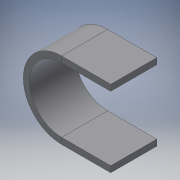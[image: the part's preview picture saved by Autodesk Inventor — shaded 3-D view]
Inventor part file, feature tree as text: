
AUTODESK INVENTOR PART (.ipt)
format: ipt  version: 2018 (Build 220112000, 112)  size: 137,216 bytes
history: native  units: mm
features: sheet_metal_op x3, other x2, sketch x1
ambient origin geometry x8: Origin, YZ Plane, XZ Plane, XY Plane, X Axis, Y Axis, Z Axis, Center Point
bodies: Solid1 (feature_tree)
feature tree (6):
  sheet_metal_op  "Contour Flange1"
  sketch  "Sketch1"  dims[d0=4.0mm d1=4.0mm d2=2.0mm d3=8.0mm d4=4.0mm d5=30.0mm d6=4.0mm d7=0.5mm d8=16.0mm d9=4.0mm d10=4.0mm d11=50.0mm d12=32.0mm]
  other  "Plate1"
  sheet_metal_op  "Bend1"
  sheet_metal_op  "Corner1"
  other  "Definition1"
